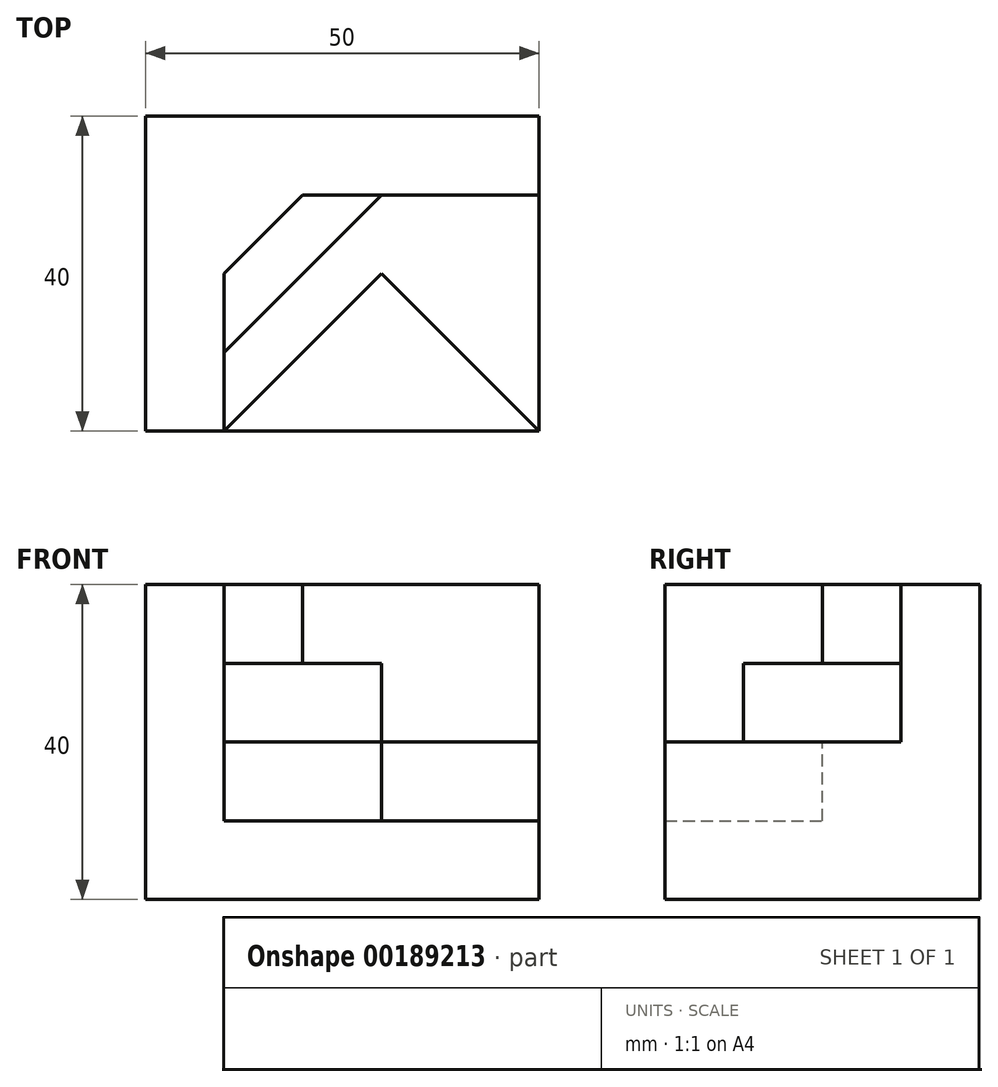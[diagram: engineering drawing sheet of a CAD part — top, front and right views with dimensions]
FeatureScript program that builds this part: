
annotation { "Feature Type Name" : "Feature", "Feature Type Description" : "" }
export const myFeature = defineFeature(function(context is Context, id is Id, definition is map)
    precondition{}
    {
        {
            var Q0;
            Q0=qCreatedBy(makeId("Top.planeOp"),FACE);
            var sketch = newSketch(context, id + "F0", { "sketchPlane" : qUnion([Q0])});
            skLineSegment(sketch, "E0.bottom", {"start": v(0, 0) * mm, "end": v(50, 0) * mm});
            skLineSegment(sketch, "E0.top", {"start": v(0, 40) * mm, "end": v(50, 40) * mm});
            skLineSegment(sketch, "E0.left", {"start": v(0, 0) * mm, "end": v(0, 40) * mm});
            skLineSegment(sketch, "E0.right", {"start": v(50, 0) * mm, "end": v(50, 40) * mm});
            skSolve(sketch);
        }
        {
            var Q0;
            Q0=makeQuery(id+"F0.imprint","IMPRINT",FACE,{"disambiguationData":[TD([[makeQuery(id+"F0.imprint","IMPRINT",EDGE,{"derivedFrom":sQuery(id+"F0.wireOp",EDGE,"E0.bottom")}),1.0]])]});
            extrude(context, id + "F1", {"entities" : qUnion([Q0]), "depth" : 40 * mm});
        }
        {
            var Q0;
            Q0=makeQuery(id+"F1.opExtrude","CAP_FACE",FACE,{"disambiguationData":[OSD([sQuery(id+"F0.wireOp",EDGE,"E0.bottom"),sQuery(id+"F0.wireOp",EDGE,"E0.top"),sQuery(id+"F0.wireOp",EDGE,"E0.left"),sQuery(id+"F0.wireOp",EDGE,"E0.right")])],"isStart":false});
            var sketch = newSketch(context, id + "F2", { "sketchPlane" : qUnion([Q0])});
            skLineSegment(sketch, "E1", {"start": v(10, 0) * mm, "end": v(10, 20) * mm});
            skLineSegment(sketch, "E2", {"start": v(20, 30) * mm, "end": v(50, 30) * mm});
            skLineSegment(sketch, "E3.0", {"start": v(10, 0) * mm, "end": v(50, 0) * mm});
            skLineSegment(sketch, "E4.0", {"start": v(50, 0) * mm, "end": v(50, 30) * mm});
            skLineSegment(sketch, "E5", {"start": v(10, 20) * mm, "end": v(20, 30) * mm});
            skPoint(sketch, "E6.orphan", {"position": v(0, 0) * mm});
            skPoint(sketch, "E7.orphan", {"position": v(50, 40) * mm});
            skSolve(sketch);
        }
        {
            var Q0;
            Q0=makeQuery(id+"F2.imprint","IMPRINT",FACE,{"disambiguationData":[TD([[makeQuery(id+"F2.imprint","IMPRINT",EDGE,{"derivedFrom":sQuery(id+"F2.wireOp",EDGE,"E1")}),-1.0]])]});
            extrude(context, id + "F3", {"entities" : qUnion([Q0]), "operationType" : NewBodyOperationType.REMOVE, "oppositeDirection" : true, "depth" : 10 * mm});
        }
        {
            var Q0;
            Q0=makeQuery(id+"F3.boolean.opBoolean","COPY",FACE,{"derivedFrom":makeQuery(id+"F3.opExtrude","CAP_FACE",FACE,{"disambiguationData":[OSD([sQuery(id+"F2.wireOp",EDGE,"E1"),sQuery(id+"F2.wireOp",EDGE,"E2"),sQuery(id+"F2.wireOp",EDGE,"E3.0"),sQuery(id+"F2.wireOp",EDGE,"E4.0"),sQuery(id+"F2.wireOp",EDGE,"E5")])],"isStart":false})});
            var sketch = newSketch(context, id + "F4", { "sketchPlane" : qUnion([Q0])});
            skLineSegment(sketch, "E8.0", {"start": v(10, 0) * mm, "end": v(10, 10) * mm});
            skLineSegment(sketch, "E9.0", {"start": v(30, 30) * mm, "end": v(50, 30) * mm});
            skPoint(sketch, "E10.0", {"position": v(50, 15) * mm});
            skLineSegment(sketch, "E11.0", {"start": v(10, 0) * mm, "end": v(50, 0) * mm});
            skLineSegment(sketch, "E12.0", {"start": v(50, 0) * mm, "end": v(50, 30) * mm});
            skLineSegment(sketch, "E13", {"start": v(10, 10) * mm, "end": v(30, 30) * mm});
            skPoint(sketch, "E14.orphan", {"position": v(10, 20) * mm});
            skPoint(sketch, "E15.orphan", {"position": v(20, 30) * mm});
            skSolve(sketch);
        }
        {
            var Q0;
            Q0=makeQuery(id+"F4.imprint","IMPRINT",FACE,{"disambiguationData":[TD([[makeQuery(id+"F4.imprint","IMPRINT",EDGE,{"derivedFrom":sQuery(id+"F4.wireOp",EDGE,"E8.0")}),-1.0]])]});
            extrude(context, id + "F5", {"entities" : qUnion([Q0]), "operationType" : NewBodyOperationType.REMOVE, "oppositeDirection" : true, "depth" : 10 * mm});
        }
        {
            var Q0;
            Q0=makeQuery(id+"F5.boolean.opBoolean","COPY",FACE,{"derivedFrom":makeQuery(id+"F5.opExtrude","CAP_FACE",FACE,{"disambiguationData":[OSD([sQuery(id+"F4.wireOp",EDGE,"E8.0"),sQuery(id+"F4.wireOp",EDGE,"E9.0"),sQuery(id+"F4.wireOp",EDGE,"E11.0"),sQuery(id+"F4.wireOp",EDGE,"E12.0"),sQuery(id+"F4.wireOp",EDGE,"E13")])],"isStart":false})});
            var sketch = newSketch(context, id + "F6", { "sketchPlane" : qUnion([Q0])});
            skLineSegment(sketch, "E16.0", {"start": v(10, 0) * mm, "end": v(50, 0) * mm});
            skLineSegment(sketch, "E17", {"start": v(10, 0) * mm, "end": v(30, 20) * mm});
            skLineSegment(sketch, "E18", {"start": v(30, 20) * mm, "end": v(50, 0) * mm});
            skSolve(sketch);
        }
        {
            var Q0;
            Q0=makeQuery(id+"F6.imprint","IMPRINT",FACE,{"disambiguationData":[TD([[makeQuery(id+"F6.imprint","IMPRINT",EDGE,{"derivedFrom":sQuery(id+"F6.wireOp",EDGE,"E16.0")}),1.0]])]});
            extrude(context, id + "F7", {"entities" : qUnion([Q0]), "operationType" : NewBodyOperationType.REMOVE, "oppositeDirection" : true, "depth" : 10 * mm});
        }
    });
